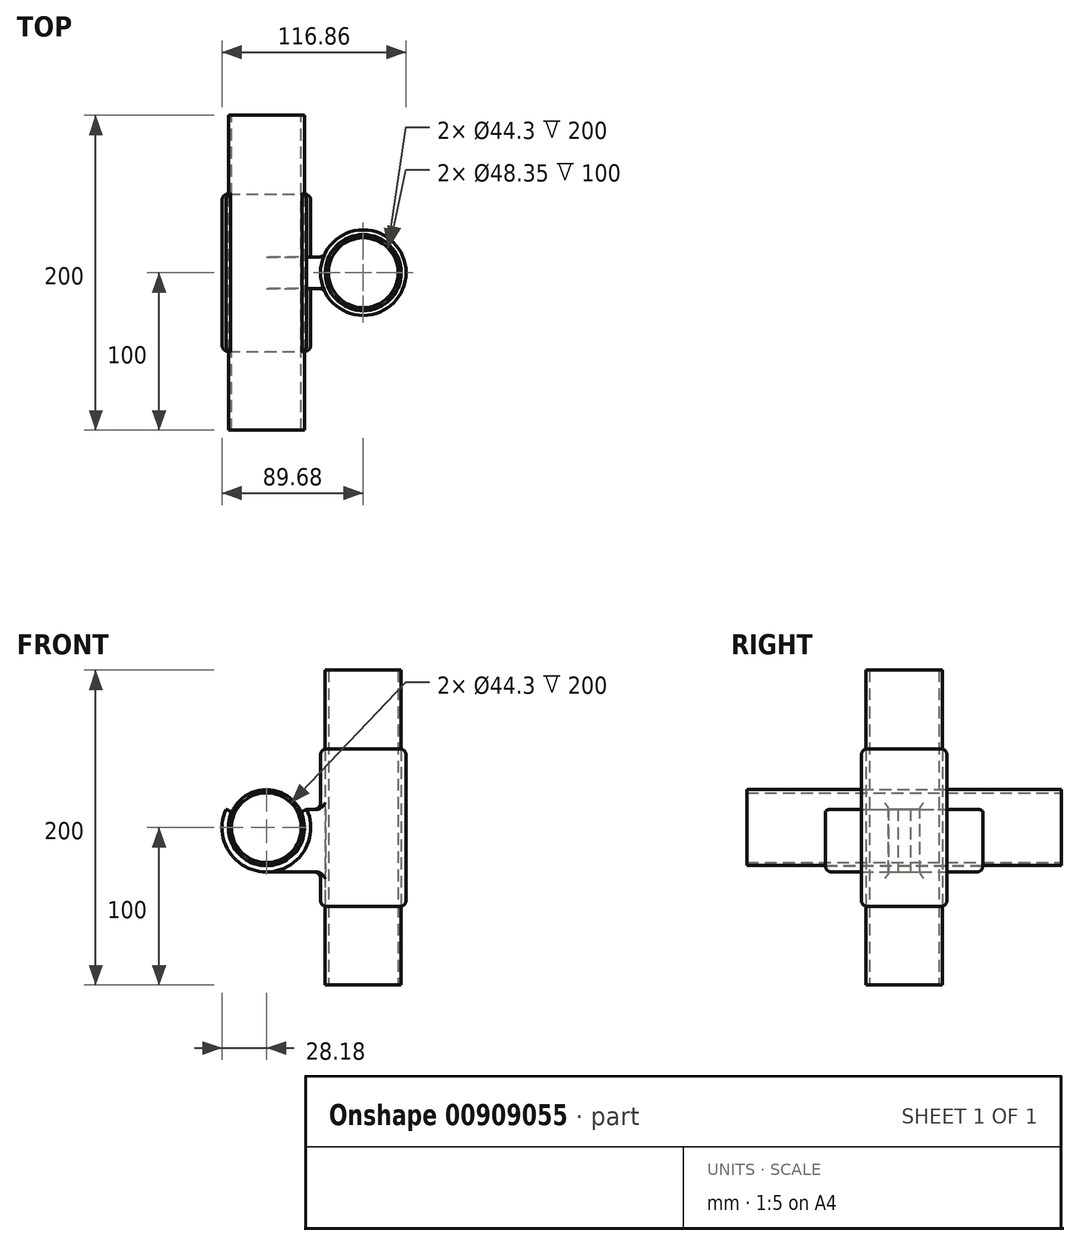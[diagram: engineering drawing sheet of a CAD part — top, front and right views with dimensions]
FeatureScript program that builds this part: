
annotation { "Feature Type Name" : "Feature", "Feature Type Description" : "" }
export const myFeature = defineFeature(function(context is Context, id is Id, definition is map)
    precondition{}
    {
        {
            var Q0;
            Q0=qCreatedBy(makeId("Top.planeOp"),FACE);
            var sketch = newSketch(context, id + "F0", { "sketchPlane" : qUnion([Q0])});
            skCircle(sketch, "E0", {"center": v(0, 0) * mm, "radius": 24.15 * mm});
            skCircle(sketch, "E1", {"center": v(0, 0) * mm, "radius": 22.15 * mm});
            skSolve(sketch);
        }
        {
            var Q0;
            Q0 = qSketchRegion(id + "F0", true);
            extrude(context, id + "F1", {"entities" : qUnion([Q0]), "endBound" : BoundingType.SYMMETRIC, "depth" : 200 * mm, "offsetDistance" : 25 * mm});
        }
        {
            var Q0;
            Q0=qCreatedBy(makeId("Top.planeOp"),FACE);
            var sketch = newSketch(context, id + "F2", { "sketchPlane" : qUnion([Q0])});
            skCircle(sketch, "E2", {"center": v(0, 0) * mm, "radius": 24.18 * mm});
            skCircle(sketch, "E3", {"center": v(0, 0) * mm, "radius": 27.18 * mm});
            skSolve(sketch);
        }
        {
            var Q0;
            Q0=makeQuery(id+"F2.imprint","IMPRINT",FACE,{"disambiguationData":[TD([[makeQuery(id+"F2.imprint","IMPRINT",EDGE,{"derivedFrom":sQuery(id+"F2.wireOp",EDGE,"E2")}),-1.0]])]});
            extrude(context, id + "F3", {"entities" : qUnion([Q0]), "endBound" : BoundingType.SYMMETRIC, "depth" : 100 * mm, "offsetDistance" : 25 * mm});
        }
        {
            var Q0;
            Q0=qCreatedBy(makeId("Front.planeOp"),FACE);
            var sketch = newSketch(context, id + "F4", { "sketchPlane" : qUnion([Q0])});
            skCircle(sketch, "E4", {"center": v(-61.5, 0) * mm, "radius": 24.15 * mm});
            skCircle(sketch, "E5", {"center": v(-61.5, 0) * mm, "radius": 22.15 * mm});
            skSolve(sketch);
        }
        {
            var Q0;
            Q0 = qSketchRegion(id + "F4", true);
            extrude(context, id + "F5", {"entities" : qUnion([Q0]), "endBound" : BoundingType.SYMMETRIC, "depth" : 200 * mm, "offsetDistance" : 25 * mm});
        }
        {
            var Q0;
            Q0=qCreatedBy(makeId("Front.planeOp"),FACE);
            var sketch = newSketch(context, id + "F6", { "sketchPlane" : qUnion([Q0])});
            skPoint(sketch, "E6", {"position": v(-61.5, 0) * mm});
            skArc(sketch, "E7", {"start": v(-84.2, 8.29) * mm, "mid": v(-61.5, -24.18) * mm, "end": v(-38.8, 8.29) * mm});
            skLineSegment(sketch, "E8", {"start": v(-61.5, 0) * mm, "end": v(0, 0) * mm, "construction": true});
            skArc(sketch, "E9.0", {"start": v(-87.15, 11.65) * mm, "mid": v(-61.5, -28.18) * mm, "end": v(-35.85, 11.65) * mm});
            skLineSegment(sketch, "E10", {"start": v(-85.26, 10.8) * mm, "end": v(-87.15, 11.65) * mm});
            skLineSegment(sketch, "E11", {"start": v(-37.74, 10.8) * mm, "end": v(-35.85, 11.65) * mm});
            skPoint(sketch, "E12.visualSharp", {"position": v(-83.5, 10) * mm});
            skArc(sketch, "E12.filletArc", {"start": v(-84.2, 8.29) * mm, "mid": v(-84.24, 9.75) * mm, "end": v(-85.26, 10.8) * mm});
            skPoint(sketch, "E13.visualSharp", {"position": v(-39.5, 10) * mm});
            skArc(sketch, "E13.filletArc", {"start": v(-37.74, 10.8) * mm, "mid": v(-38.76, 9.75) * mm, "end": v(-38.8, 8.29) * mm});
            skSolve(sketch);
        }
        {
            var Q0;
            Q0 = qSketchRegion(id + "F6", true);
            extrude(context, id + "F7", {"entities" : qUnion([Q0]), "endBound" : BoundingType.SYMMETRIC, "depth" : 100 * mm, "offsetDistance" : 25 * mm});
        }
        {
            var Q0;
            Q0=qCreatedBy(makeId("Front.planeOp"),FACE);
            var sketch = newSketch(context, id + "F8", { "sketchPlane" : qUnion([Q0])});
            skLineSegment(sketch, "E14", {"start": v(-35.85, 11.65) * mm, "end": v(-23.85, 11.65) * mm});
            skLineSegment(sketch, "E15", {"start": v(-23.85, 11.65) * mm, "end": v(-23.85, -28.18) * mm});
            skLineSegment(sketch, "E16", {"start": v(-23.85, -28.18) * mm, "end": v(-61.5, -28.18) * mm});
            skArc(sketch, "E17", {"start": v(-61.5, -28.18) * mm, "mid": v(-37.81, -15.26) * mm, "end": v(-35.85, 11.65) * mm});
            skSolve(sketch);
        }
        {
            var Q0;
            Q0 = qSketchRegion(id + "F8", true);
            extrude(context, id + "F9", {"entities" : qUnion([Q0]), "endBound" : BoundingType.SYMMETRIC, "depth" : 20 * mm, "offsetDistance" : 25 * mm});
        }
        {
            var Q0;
            Q0=makeQuery(id+"F7.opExtrude","SWEPT_BODY",BODY,{"disambiguationData":[OSD([sQuery(id+"F6.wireOp",EDGE,"E7"),sQuery(id+"F6.wireOp",EDGE,"E9.0"),sQuery(id+"F6.wireOp",EDGE,"E10"),sQuery(id+"F6.wireOp",EDGE,"E11"),sQuery(id+"F6.wireOp",EDGE,"E12.filletArc"),sQuery(id+"F6.wireOp",EDGE,"E13.filletArc")])]});
            var Q1;
            Q1=makeQuery(id+"F9.opExtrude","SWEPT_BODY",BODY,{"disambiguationData":[OSD([sQuery(id+"F8.wireOp",EDGE,"E14"),sQuery(id+"F8.wireOp",EDGE,"E15"),sQuery(id+"F8.wireOp",EDGE,"E16"),sQuery(id+"F8.wireOp",EDGE,"E17")])]});
            var Q2;
            Q2=makeQuery(id+"F3.opExtrude","SWEPT_BODY",BODY,{"disambiguationData":[OSD([sQuery(id+"F2.wireOp",EDGE,"E2"),sQuery(id+"F2.wireOp",EDGE,"E3")])]});
            booleanBodies(context, id + "F10", {"operationType" : BooleanOperationType.UNION, "tools" : qUnion([Q0, Q1, Q2])});
        }
        {
            var Q0;
            Q0=makeQuery(id+"F10.opBoolean","INTERSECT",EDGE,{"derivedFrom":[makeQuery(id+"F3.opExtrude","SWEPT_FACE",FACE,{"disambiguationData":[OSD([sQuery(id+"F2.wireOp",EDGE,"E3")])]}),makeQuery(id+"F9.opExtrude","CAP_FACE",FACE,{"disambiguationData":[OSD([sQuery(id+"F8.wireOp",EDGE,"E14"),sQuery(id+"F8.wireOp",EDGE,"E15"),sQuery(id+"F8.wireOp",EDGE,"E16"),sQuery(id+"F8.wireOp",EDGE,"E17")])],"isStart":false})]});
            var Q1;
            Q1=makeQuery(id+"F7.opExtrude","CAP_EDGE",EDGE,{"disambiguationData":[OSD([sQuery(id+"F6.wireOp",EDGE,"E9.0")])],"isStart":false});
            var Q2;
            Q2=makeQuery(id+"F7.opExtrude","CAP_EDGE",EDGE,{"disambiguationData":[OSD([sQuery(id+"F6.wireOp",EDGE,"E9.0")])],"isStart":true});
            var Q3;
            Q3=makeQuery(id+"F9.opExtrude","CAP_EDGE",EDGE,{"disambiguationData":[OSD([sQuery(id+"F8.wireOp",EDGE,"E17")])],"isStart":true});
            var Q4;
            Q4=makeQuery(id+"F10.opBoolean","INTERSECT",EDGE,{"derivedFrom":[makeQuery(id+"F3.opExtrude","SWEPT_FACE",FACE,{"disambiguationData":[OSD([sQuery(id+"F2.wireOp",EDGE,"E3")])]}),makeQuery(id+"F9.opExtrude","CAP_FACE",FACE,{"disambiguationData":[OSD([sQuery(id+"F8.wireOp",EDGE,"E14"),sQuery(id+"F8.wireOp",EDGE,"E15"),sQuery(id+"F8.wireOp",EDGE,"E16"),sQuery(id+"F8.wireOp",EDGE,"E17")])],"isStart":true})]});
            var Q5;
            Q5=makeQuery(id+"F9.opExtrude","CAP_EDGE",EDGE,{"disambiguationData":[OSD([sQuery(id+"F8.wireOp",EDGE,"E17")])],"isStart":false});
            var Q6;
            Q6=makeQuery(id+"F9.opExtrude","SWEPT_EDGE",EDGE,{"disambiguationData":[OSD([sQuery(id+"F8.wireOp",EDGE,"E16"),sQuery(id+"F8.wireOp",EDGE,"E17")])]});
            var Q7;
            Q7=makeQuery(id+"F10.opBoolean","INTERSECT",EDGE,{"derivedFrom":[makeQuery(id+"F3.opExtrude","SWEPT_FACE",FACE,{"disambiguationData":[OSD([sQuery(id+"F2.wireOp",EDGE,"E3")])]}),makeQuery(id+"F9.opExtrude","SWEPT_FACE",FACE,{"disambiguationData":[OSD([sQuery(id+"F8.wireOp",EDGE,"E16")])]})]});
            var Q8;
            Q8=makeQuery(id+"F10.opBoolean","INTERSECT",EDGE,{"derivedFrom":[makeQuery(id+"F3.opExtrude","SWEPT_FACE",FACE,{"disambiguationData":[OSD([sQuery(id+"F2.wireOp",EDGE,"E3")])]}),makeQuery(id+"F9.opExtrude","SWEPT_FACE",FACE,{"disambiguationData":[OSD([sQuery(id+"F8.wireOp",EDGE,"E14")])]})]});
            var Q9;
            Q9=makeQuery(id+"F3.opExtrude","CAP_EDGE",EDGE,{"disambiguationData":[OSD([sQuery(id+"F2.wireOp",EDGE,"E3")])],"isStart":false});
            var Q10;
            Q10=makeQuery(id+"F3.opExtrude","CAP_EDGE",EDGE,{"disambiguationData":[OSD([sQuery(id+"F2.wireOp",EDGE,"E3")])],"isStart":true});
            fillet(context, id + "F11", {"entities" : qUnion([Q0, Q1, Q2, Q3, Q4, Q5, Q6, Q7, Q8, Q9, Q10]), "radius" : 4 * mm, "tangentPropagation" : true, "allowEdgeOverflow" : false});
        }
    });
